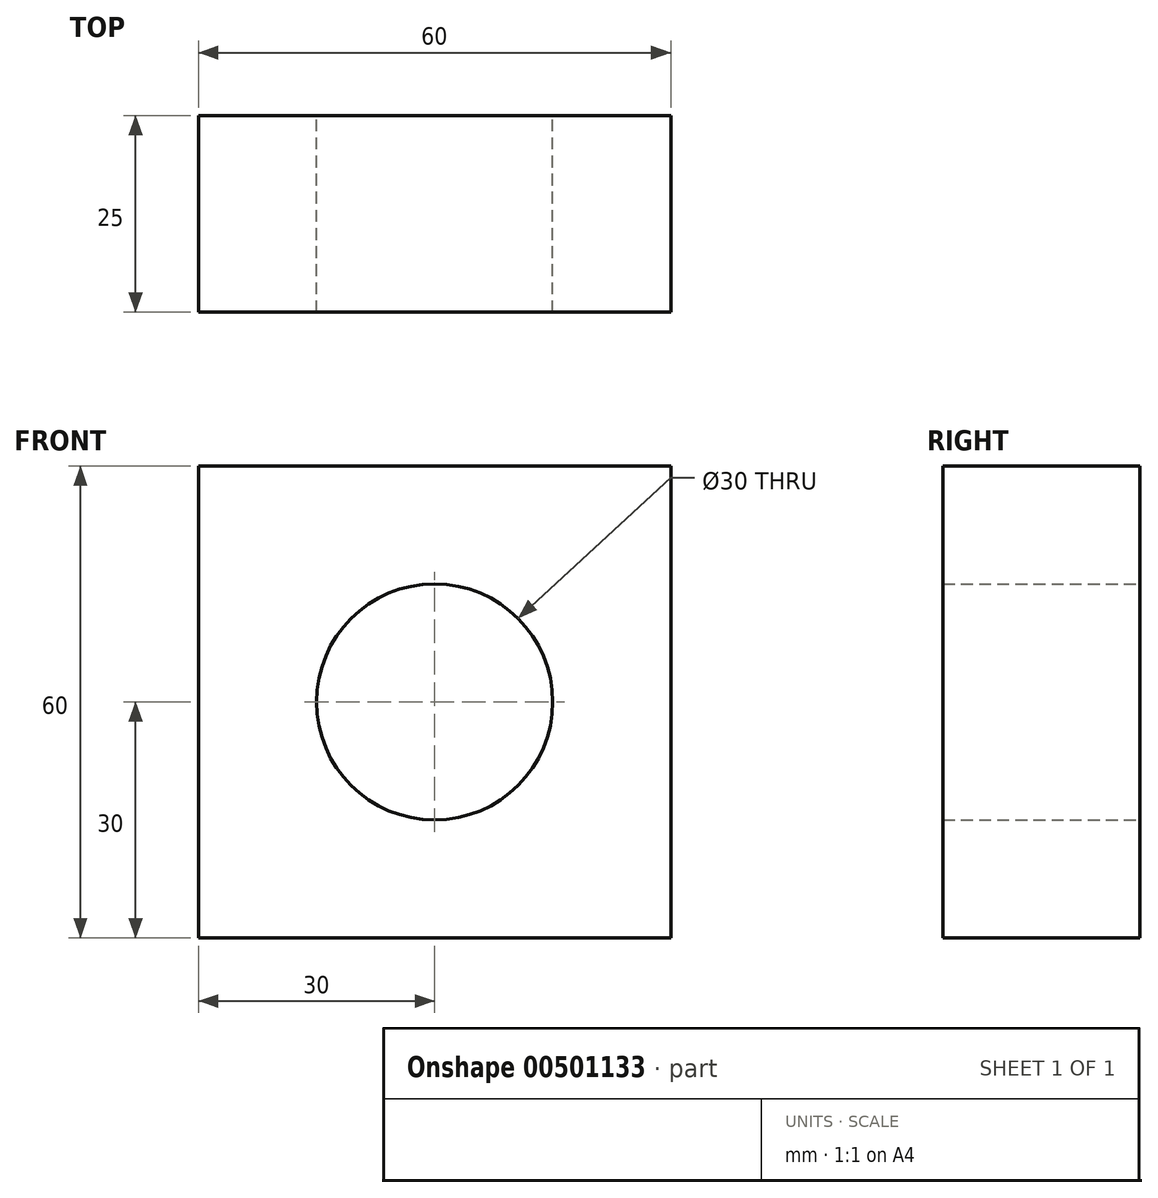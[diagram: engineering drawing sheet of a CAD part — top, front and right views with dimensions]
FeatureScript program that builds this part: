
annotation { "Feature Type Name" : "Feature", "Feature Type Description" : "" }
export const myFeature = defineFeature(function(context is Context, id is Id, definition is map)
    precondition{}
    {
        {
            var Q0;
            Q0=qCreatedBy(makeId("Front.planeOp"),FACE);
            var sketch = newSketch(context, id + "F0", { "sketchPlane" : qUnion([Q0])});
            skCircle(sketch, "E0", {"center": v(0, 0) * mm, "radius": 15 * mm});
            skLineSegment(sketch, "E1.bottom", {"start": v(-30, 30) * mm, "end": v(30, 30) * mm});
            skLineSegment(sketch, "E1.top", {"start": v(-30, -30) * mm, "end": v(30, -30) * mm});
            skLineSegment(sketch, "E1.left", {"start": v(-30, 30) * mm, "end": v(-30, -30) * mm});
            skLineSegment(sketch, "E1.right", {"start": v(30, 30) * mm, "end": v(30, -30) * mm});
            skSolve(sketch);
        }
        {
            var Q0;
            Q0 = qSketchRegion(id + "F0", true);
            extrude(context, id + "F1", {"entities" : qUnion([Q0]), "depth" : 25 * mm});
        }
    });
